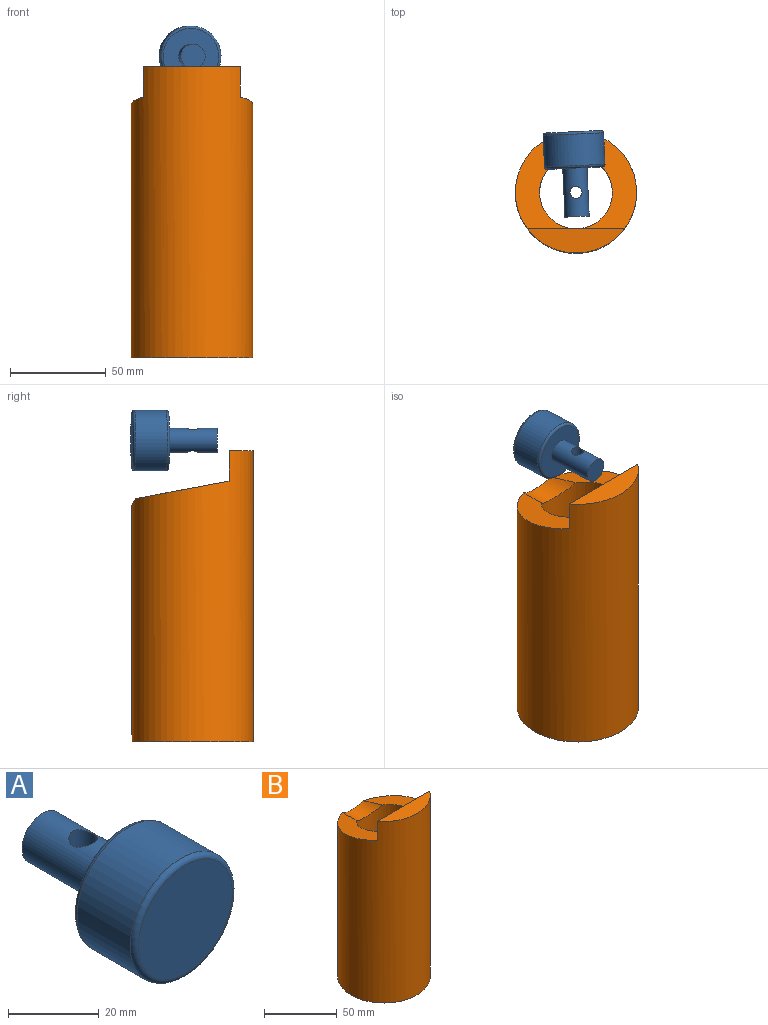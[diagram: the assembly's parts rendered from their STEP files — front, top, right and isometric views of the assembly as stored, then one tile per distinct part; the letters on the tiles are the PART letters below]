
ASSEMBLY  parts=2 mates=1
PART A: 8 faces, bbox 34.4x44.5x34.4 mm
  f0: cylinder r=15.88mm len=31.75mm, axis (0,-1,0), area 1646.8mm2, adj f3,f4
  f1: plane 29.21x29.21mm, normal (0,1,0), area 543.4mm2, adj f4,f5
  f2: plane 29.21x29.21mm, normal (0,-1,0), area 670.1mm2, adj f3
  f3: torus R=14.61mm, axis (0,-1,0), area 193.2mm2, adj f0,f2
  f4: torus R=14.61mm, axis (0,-1,0), area 193.2mm2, adj f0,f1
  f5: cylinder r=6.35mm len=25.4mm, axis (0,-1,0), area 948.1mm2, adj f1,f6,f7
  f6: plane 12.7x12.7mm, normal (0,1,0), area 126.7mm2, adj f5
  f7: cylinder r=3.17mm len=12.7mm, axis (0,0,1), area 236.7mm2, adj f5
PART B: 8 faces, bbox 63.5x63.5x152.4 mm
  f0: plane 49.21x31.75mm, normal (0,0.18,0.98), area 647.6mm2, adj f1,f2,f6,f7
  f1: cylinder r=19.05mm len=136.53mm, axis (0,0,1), area 15808.2mm2, adj f0,f3,f5,f7
  f2: cylinder r=31.75mm len=152.4mm, axis (0,0,1), area 27322.2mm2, adj f0,f3,f4,f5,f6,f7
  f3: plane 63.5x63.5mm, normal (0,0,-1), area 2026.8mm2, adj f1,f2
  f4: plane 50.8x12.7mm, normal (0,0,1), area 450.9mm2, adj f2,f6
  f5: plane 49.21x31.75mm, normal (0,0.18,0.98), area 647.6mm2, adj f1,f2,f6,f7
  f6: plane 50.8x15.88mm, normal (0,1,0), area 806.4mm2, adj f0,f2,f4,f5
  f7: cylinder r=15.88mm len=25.6mm, axis (0,-1,0), area 341.2mm2, adj f0,f1,f2,f5
PLACE A rot(axis=(0,0,-1),177.4deg) t=(73.9,-162.91,136.23)mm
PLACE B t=(75.36,-194.63,130.75)mm fixed
MATE cylindrical A.f7 <-> B.f1  axis (0,0,1) through (75.36,-194.63,129.79)mm
